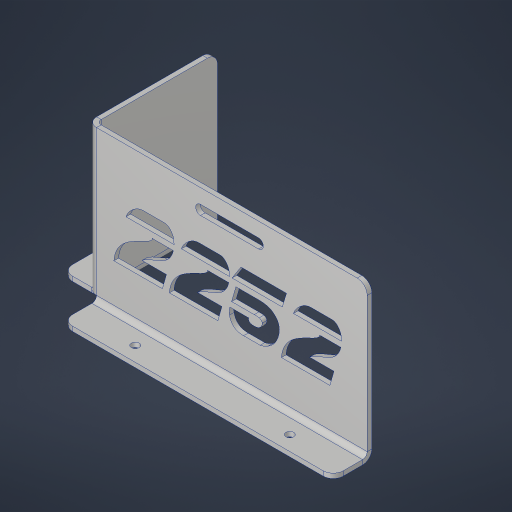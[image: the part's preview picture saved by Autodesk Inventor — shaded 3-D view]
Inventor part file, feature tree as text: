
AUTODESK INVENTOR PART (.ipt)
format: ipt  version: 2023.4 (Build 274418000, 418)  size: 537,088 bytes
history: native  units: in
note: dims shown in document units (in); Inventor stores cm internally (conversion verified against a paired STEP export)
features: sheet_metal_op x7, sketch x6, other x5, emboss x1, hole x1, fillet x1
ambient origin geometry x8: Origin, YZ Plane, XZ Plane, XY Plane, X Axis, Y Axis, Z Axis, Center Point
bodies: Solid1 (feature_tree)
feature tree (21):
  sheet_metal_op  "Face1"
  sheet_metal_op  "Flange1"
  sheet_metal_op  "Flange2"
  emboss  "Emboss1"
  hole  "Hole1"  [1 undecoded]
  fillet  "Fillet1"  Radius=0.12in
  sketch  "Sketch1"  dims[d0=7.125in d1=4.0in d2=0.12in]
  other  "Plate1"
  sketch  "Sketch2"  dims[d3=0.12in]
  other  "Plate2"
  sheet_metal_op  "Bend1"
  sheet_metal_op  "Corner1"
  sketch  "Sketch3"  dims[d4=0.06in]
  other  "Plate3"
  sheet_metal_op  "Bend2"
  sheet_metal_op  "Corner2"
  sketch  "Sketch4"  dims[d5=0.24in]
  sketch  "Sketch5"  dims[d6=0.12in]
  sketch  "Sketch6"  dims[d7=3.25in d8=90.0deg d9=0.12in d10=0.48in d11=0.12in d12=0.12in d13=0.12in d14=0.06in d15=0.24in d16=0.12in d17=1.0in d18=90.0deg d19=0.12in d20=0.48in d21=0.12in d22=0.12in d24=0.25in d25=1.5in d26=0.5in d27=0.12in d28=0.0in d29=0.25in d30=0.0in d31=1.5in d32=4.0in d33=0.201in d34=0.38in d35=0.385in d36=0.25in d37=0.5635in d38=0.12in d39=0.8108in d40=0.26in]
  other  "Cut1"
  other  "Definition1"
note: 1 required parameter value undecoded (feature->parameter linkage not recoverable at this tier; creation-order binding heuristic only, values carry confidence <= 0.55)
